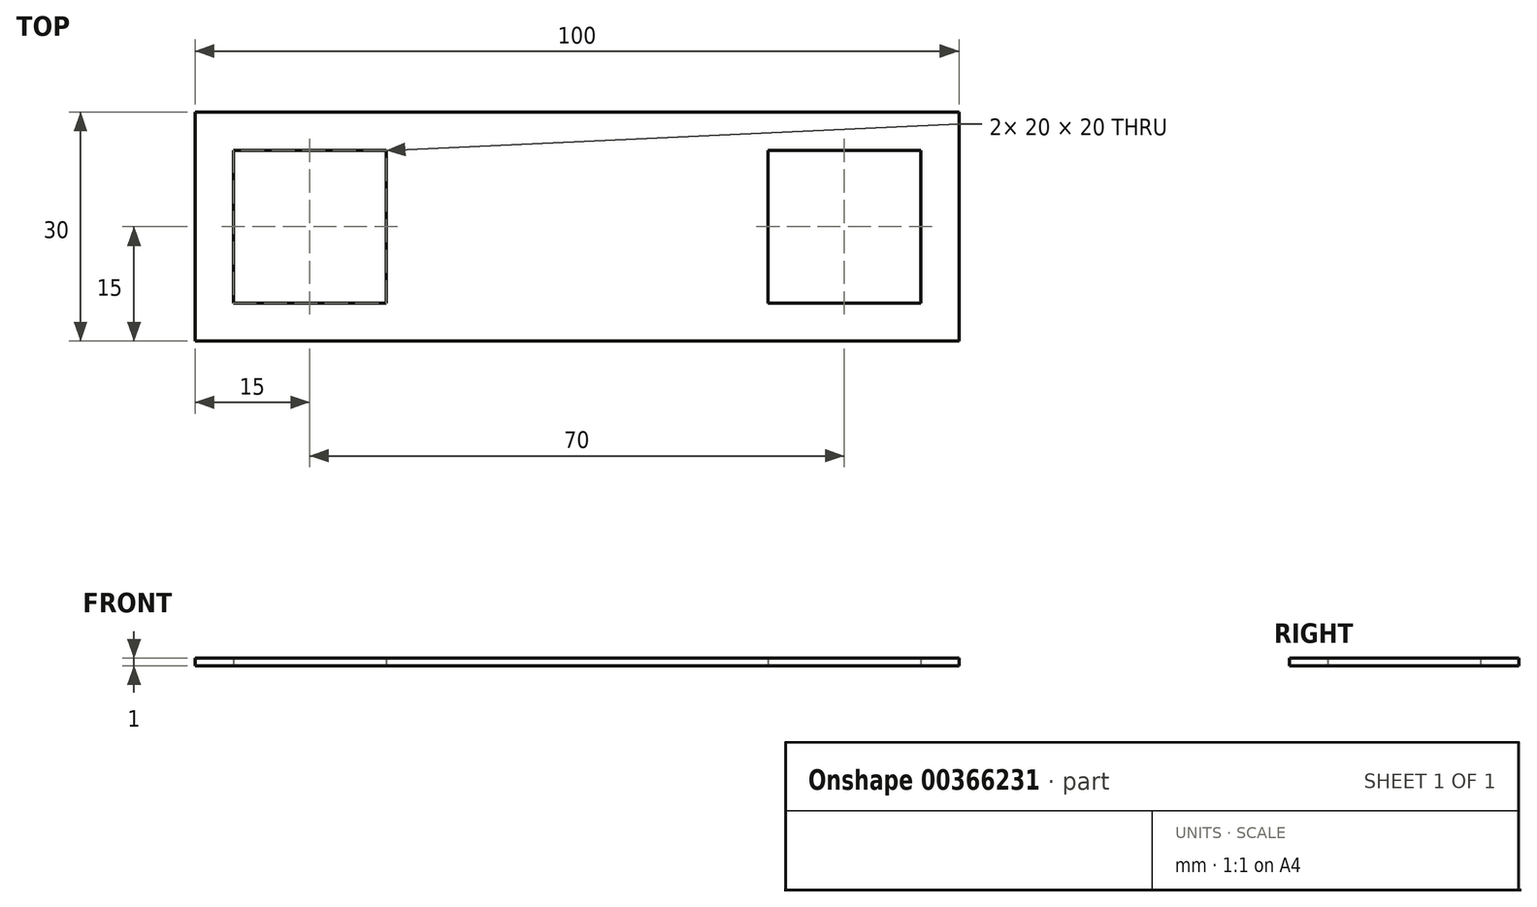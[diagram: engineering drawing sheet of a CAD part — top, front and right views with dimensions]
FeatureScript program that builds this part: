
annotation { "Feature Type Name" : "Feature", "Feature Type Description" : "" }
export const myFeature = defineFeature(function(context is Context, id is Id, definition is map)
    precondition{}
    {
        {
            var Q0;
            Q0=qCreatedBy(makeId("Top.planeOp"),FACE);
            var sketch = newSketch(context, id + "F0", { "sketchPlane" : qUnion([Q0])});
            skLineSegment(sketch, "E0.bottom", {"start": v(50, 15) * mm, "end": v(-50, 15) * mm});
            skLineSegment(sketch, "E0.top", {"start": v(50, -15) * mm, "end": v(-50, -15) * mm});
            skLineSegment(sketch, "E0.left", {"start": v(50, 15) * mm, "end": v(50, -15) * mm});
            skLineSegment(sketch, "E0.right", {"start": v(-50, 15) * mm, "end": v(-50, -15) * mm});
            skPoint(sketch, "E0.middle", {"position": v(0, 0) * mm});
            skLineSegment(sketch, "E1.bottom", {"start": v(-25, 10) * mm, "end": v(-45, 10) * mm});
            skLineSegment(sketch, "E1.top", {"start": v(-25, -10) * mm, "end": v(-45, -10) * mm});
            skLineSegment(sketch, "E1.left", {"start": v(-25, 10) * mm, "end": v(-25, -10) * mm});
            skLineSegment(sketch, "E1.right", {"start": v(-45, 10) * mm, "end": v(-45, -10) * mm});
            skPoint(sketch, "E1.middle", {"position": v(-35, 0) * mm});
            skLineSegment(sketch, "E2.bottom", {"start": v(45, 10) * mm, "end": v(25, 10) * mm});
            skLineSegment(sketch, "E2.top", {"start": v(45, -10) * mm, "end": v(25, -10) * mm});
            skLineSegment(sketch, "E2.left", {"start": v(45, 10) * mm, "end": v(45, -10) * mm});
            skLineSegment(sketch, "E2.right", {"start": v(25, 10) * mm, "end": v(25, -10) * mm});
            skPoint(sketch, "E2.middle", {"position": v(35, 0) * mm});
            skSolve(sketch);
        }
        {
            var Q0;
            Q0=makeQuery(id+"F0.imprint","IMPRINT",FACE,{"disambiguationData":[TD([[makeQuery(id+"F0.imprint","IMPRINT",EDGE,{"derivedFrom":sQuery(id+"F0.wireOp",EDGE,"E0.bottom")}),1.0]])]});
            extrude(context, id + "F1", {"entities" : qUnion([Q0]), "depth" : 1 * mm});
        }
    });
